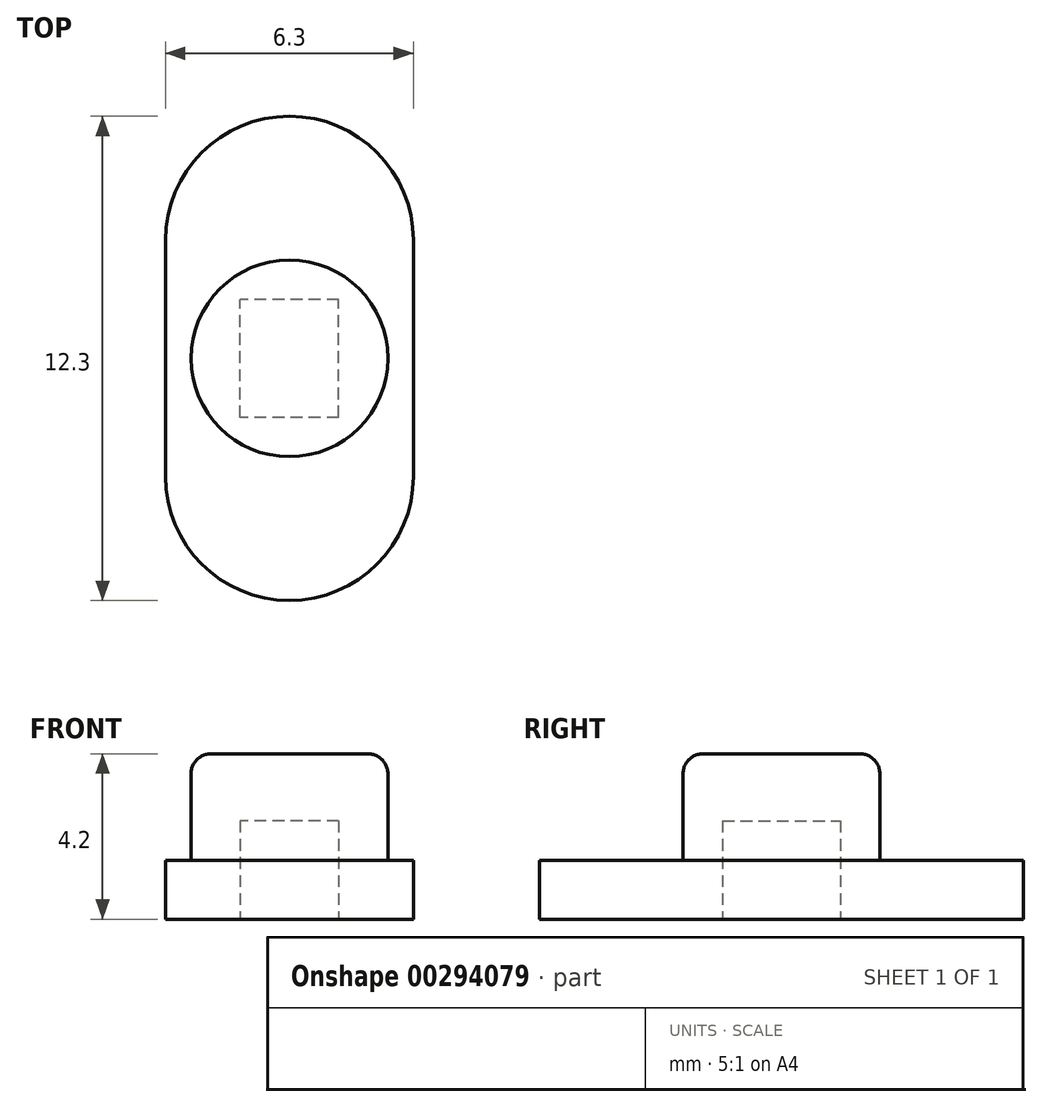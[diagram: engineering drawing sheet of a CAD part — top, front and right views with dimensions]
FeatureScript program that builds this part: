
annotation { "Feature Type Name" : "Feature", "Feature Type Description" : "" }
export const myFeature = defineFeature(function(context is Context, id is Id, definition is map)
    precondition{}
    {
        {
            var Q0;
            Q0=qCreatedBy(makeId("Top.planeOp"),FACE);
            var sketch = newSketch(context, id + "F0", { "sketchPlane" : qUnion([Q0])});
            skArc(sketch, "E0", {"start": v(-3.15, -3) * mm, "mid": v(0, -6.15) * mm, "end": v(3.15, -3) * mm});
            skLineSegment(sketch, "E1.bottom", {"start": v(1.25, -1.5) * mm, "end": v(-1.25, -1.5) * mm});
            skLineSegment(sketch, "E1.top", {"start": v(1.25, 1.5) * mm, "end": v(-1.25, 1.5) * mm});
            skLineSegment(sketch, "E1.left", {"start": v(1.25, -1.5) * mm, "end": v(1.25, 1.5) * mm});
            skLineSegment(sketch, "E1.right", {"start": v(-1.25, -1.5) * mm, "end": v(-1.25, 1.5) * mm});
            skPoint(sketch, "E1.middle", {"position": v(0, 0) * mm});
            skLineSegment(sketch, "E2", {"start": v(-4.62, 3) * mm, "end": v(7.24, 3) * mm, "construction": true});
            skLineSegment(sketch, "E3", {"start": v(-4.2, -3) * mm, "end": v(5.98, -3) * mm, "construction": true});
            skLineSegment(sketch, "E4", {"start": v(-3.15, 3) * mm, "end": v(-3.15, -3) * mm});
            skLineSegment(sketch, "E5", {"start": v(3.15, 3) * mm, "end": v(3.15, -3) * mm});
            skArc(sketch, "E6.trimOffspring", {"start": v(3.15, 3) * mm, "mid": v(0, 6.15) * mm, "end": v(-3.15, 3) * mm});
            skCircle(sketch, "E7", {"center": v(0, 0) * mm, "radius": 2.5 * mm});
            skSolve(sketch);
        }
        {
            var Q0;
            Q0=makeQuery(id+"F0.imprint","IMPRINT",FACE,{"disambiguationData":[TD([[makeQuery(id+"F0.imprint","IMPRINT",EDGE,{"derivedFrom":sQuery(id+"F0.wireOp",EDGE,"E0")}),1.0]])]});
            var Q1;
            Q1=makeQuery(id+"F0.imprint","IMPRINT",FACE,{"disambiguationData":[TD([[makeQuery(id+"F0.imprint","IMPRINT",EDGE,{"derivedFrom":sQuery(id+"F0.wireOp",EDGE,"E1.bottom")}),1.0]])]});
            var Q2;
            Q2=makeQuery(id+"F0.imprint","IMPRINT",FACE,{"disambiguationData":[TD([[makeQuery(id+"F0.imprint","IMPRINT",EDGE,{"derivedFrom":sQuery(id+"F0.wireOp",EDGE,"E1.bottom")}),-1.0]])]});
            extrude(context, id + "F1", {"entities" : qUnion([Q0, Q1, Q2]), "depth" : 1.5 * mm});
        }
        {
            var Q0;
            Q0=makeQuery(id+"F0.imprint","IMPRINT",FACE,{"disambiguationData":[TD([[makeQuery(id+"F0.imprint","IMPRINT",EDGE,{"derivedFrom":sQuery(id+"F0.wireOp",EDGE,"E1.bottom")}),1.0]])]});
            var Q1;
            Q1=makeQuery(id+"F0.imprint","IMPRINT",FACE,{"disambiguationData":[TD([[makeQuery(id+"F0.imprint","IMPRINT",EDGE,{"derivedFrom":sQuery(id+"F0.wireOp",EDGE,"E1.bottom")}),-1.0]])]});
            extrude(context, id + "F2", {"entities" : qUnion([Q0, Q1]), "operationType" : NewBodyOperationType.ADD, "depth" : 4.2 * mm});
        }
        {
            var Q0;
            Q0=makeQuery(id+"F0.imprint","IMPRINT",FACE,{"disambiguationData":[TD([[makeQuery(id+"F0.imprint","IMPRINT",EDGE,{"derivedFrom":sQuery(id+"F0.wireOp",EDGE,"E1.bottom")}),-1.0]])]});
            extrude(context, id + "F3", {"entities" : qUnion([Q0]), "operationType" : NewBodyOperationType.REMOVE, "depth" : 2.5 * mm});
        }
        {
            var Q0;
            Q0=makeQuery(id+"F2.opExtrude","CAP_EDGE",EDGE,{"disambiguationData":[OSD([sQuery(id+"F0.wireOp",EDGE,"E7")])],"isStart":false});
            fillet(context, id + "F4", {"entities" : qUnion([Q0]), "radius" : 0.5 * mm, "tangentPropagation" : true, "allowEdgeOverflow" : false});
        }
    });
